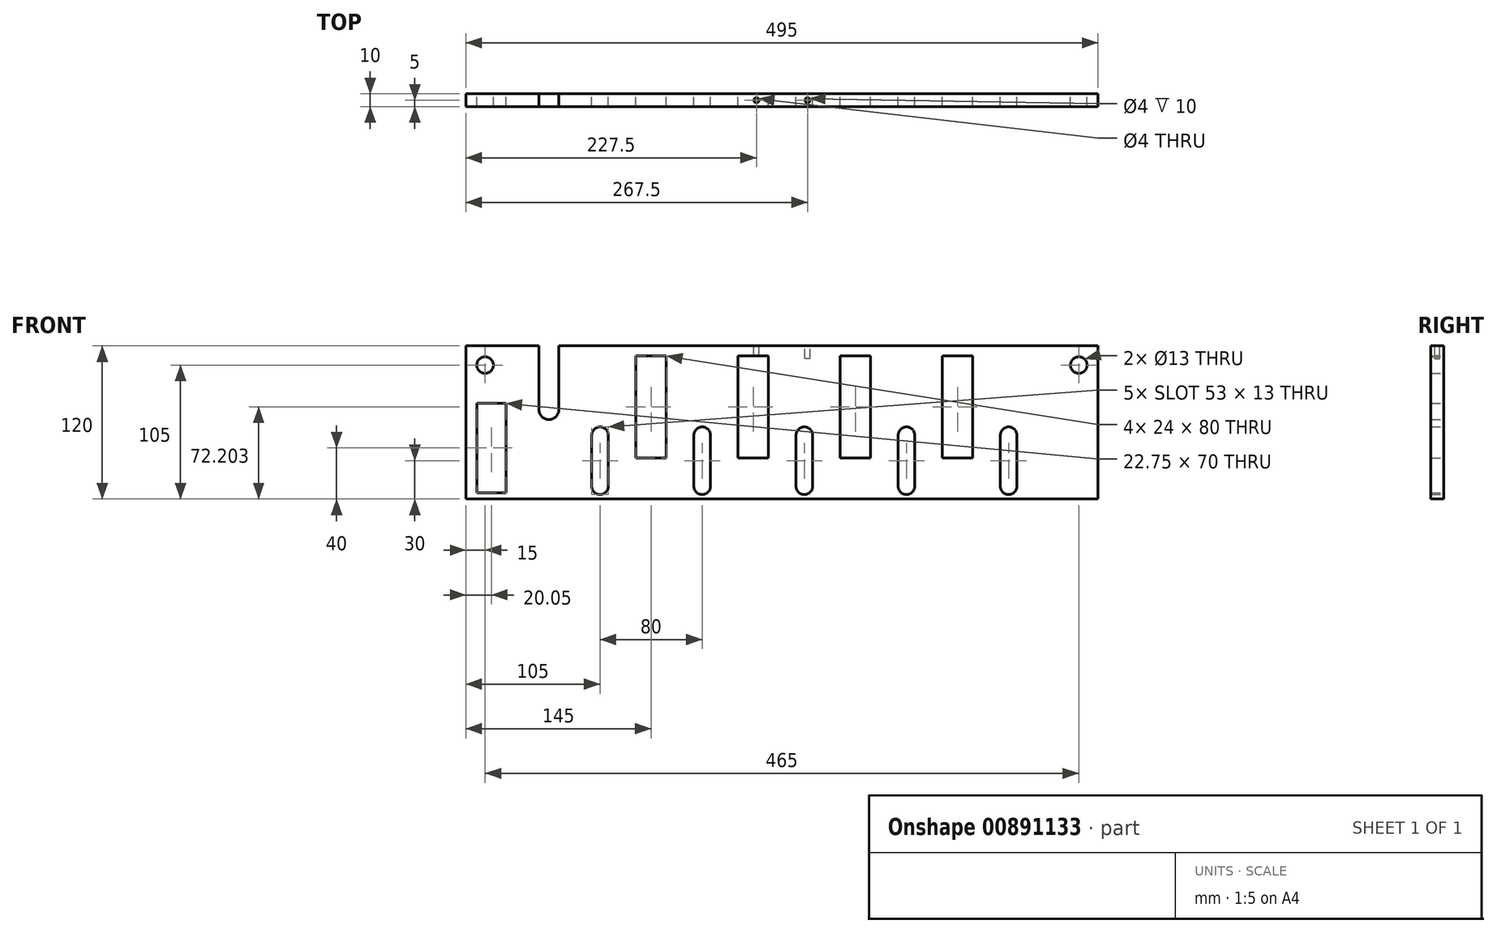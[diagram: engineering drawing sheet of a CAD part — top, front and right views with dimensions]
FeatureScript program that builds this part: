
annotation { "Feature Type Name" : "Feature", "Feature Type Description" : "" }
export const myFeature = defineFeature(function(context is Context, id is Id, definition is map)
    precondition{}
    {
        {
            var Q0;
            Q0=qCreatedBy(makeId("Front.planeOp"),FACE);
            var sketch = newSketch(context, id + "F0", { "sketchPlane" : qUnion([Q0])});
            skLineSegment(sketch, "E0.bottom", {"start": v(-247.5, -60) * mm, "end": v(247.5, -60) * mm});
            skLineSegment(sketch, "E0.top", {"start": v(-247.5, 60) * mm, "end": v(-190.25, 60) * mm});
            skLineSegment(sketch, "E0.left", {"start": v(-247.5, -60) * mm, "end": v(-247.5, 60) * mm});
            skLineSegment(sketch, "E0.right", {"start": v(247.5, -60) * mm, "end": v(247.5, 60) * mm});
            skPoint(sketch, "E0.middle", {"position": v(0, 0) * mm});
            skLineSegment(sketch, "E1", {"start": v(137.5, 131.84) * mm, "end": v(137.5, -217.37) * mm, "construction": true});
            skLineSegment(sketch, "E2", {"start": v(57.5, 134.02) * mm, "end": v(57.5, -137.51) * mm, "construction": true});
            skLineSegment(sketch, "E3", {"start": v(-22.5, 142.94) * mm, "end": v(-22.5, -137.01) * mm, "construction": true});
            skLineSegment(sketch, "E4", {"start": v(-102.5, 134.31) * mm, "end": v(-102.5, -207.96) * mm, "construction": true});
            skLineSegment(sketch, "E5.MirrorCS", {"start": v(137.5, 142.94) * mm, "end": v(137.5, -137.01) * mm, "construction": true});
            skArc(sketch, "E6", {"start": v(-190.25, 10) * mm, "mid": v(-182.5, 2.25) * mm, "end": v(-174.75, 10) * mm});
            skLineSegment(sketch, "E7", {"start": v(-190.25, 10) * mm, "end": v(-190.25, 60) * mm});
            skLineSegment(sketch, "E8", {"start": v(-174.75, 10) * mm, "end": v(-174.75, 60) * mm});
            skLineSegment(sketch, "E9", {"start": v(-149, -50) * mm, "end": v(-149, -10) * mm});
            skLineSegment(sketch, "E10", {"start": v(-136, -50) * mm, "end": v(-136, -10) * mm});
            skArc(sketch, "E11", {"start": v(-149, -10) * mm, "mid": v(-142.5, -3.5) * mm, "end": v(-136, -10) * mm});
            skArc(sketch, "E12", {"start": v(-149, -50) * mm, "mid": v(-142.5, -56.5) * mm, "end": v(-136, -50) * mm});
            skLineSegment(sketch, "E13.MirrorCS", {"start": v(-69, -50) * mm, "end": v(-69, -10) * mm});
            skArc(sketch, "E14.MirrorCS", {"start": v(-56, -10) * mm, "mid": v(-62.5, -3.5) * mm, "end": v(-69, -10) * mm});
            skLineSegment(sketch, "E15.MirrorCS", {"start": v(-56, -50) * mm, "end": v(-56, -10) * mm});
            skArc(sketch, "E16.MirrorCS", {"start": v(-56, -50) * mm, "mid": v(-62.5, -56.5) * mm, "end": v(-69, -50) * mm});
            skLineSegment(sketch, "E17.MirrorCS", {"start": v(11, -50) * mm, "end": v(11, -10) * mm});
            skLineSegment(sketch, "E18.MirrorCS", {"start": v(24, -50) * mm, "end": v(24, -10) * mm});
            skArc(sketch, "E19.MirrorCS", {"start": v(11, -10) * mm, "mid": v(17.5, -3.5) * mm, "end": v(24, -10) * mm});
            skArc(sketch, "E20.MirrorCS", {"start": v(11, -50) * mm, "mid": v(17.5, -56.5) * mm, "end": v(24, -50) * mm});
            skArc(sketch, "E21.MirrorCS", {"start": v(104, -10) * mm, "mid": v(97.5, -3.5) * mm, "end": v(91, -10) * mm});
            skLineSegment(sketch, "E22.MirrorCS", {"start": v(91, -50) * mm, "end": v(91, -10) * mm});
            skArc(sketch, "E23.MirrorCS", {"start": v(104, -50) * mm, "mid": v(97.5, -56.5) * mm, "end": v(91, -50) * mm});
            skLineSegment(sketch, "E24.MirrorCS", {"start": v(104, -50) * mm, "end": v(104, -10) * mm});
            skLineSegment(sketch, "E25.MirrorCS", {"start": v(171, -50) * mm, "end": v(171, -10) * mm});
            skLineSegment(sketch, "E26.MirrorCS", {"start": v(184, -50) * mm, "end": v(184, -10) * mm});
            skArc(sketch, "E27.MirrorCS", {"start": v(171, -10) * mm, "mid": v(177.5, -3.5) * mm, "end": v(184, -10) * mm});
            skArc(sketch, "E28.MirrorCS", {"start": v(171, -50) * mm, "mid": v(177.5, -56.5) * mm, "end": v(184, -50) * mm});
            skLineSegment(sketch, "E29.trimOffspring", {"start": v(-174.75, 60) * mm, "end": v(247.5, 60) * mm});
            skCircle(sketch, "E30", {"center": v(-232.5, 45) * mm, "radius": 6.5 * mm});
            skLineSegment(sketch, "E31", {"start": v(0, 134.05) * mm, "end": v(0, -133.19) * mm, "construction": true});
            skCircle(sketch, "E32.MirrorC", {"center": v(232.5, 45) * mm, "radius": 6.5 * mm});
            skLineSegment(sketch, "E33.bottom", {"start": v(-114.5, -27.8) * mm, "end": v(-90.5, -27.8) * mm});
            skLineSegment(sketch, "E33.top", {"start": v(-114.5, 52.2) * mm, "end": v(-90.5, 52.2) * mm});
            skLineSegment(sketch, "E33.left", {"start": v(-114.5, -27.8) * mm, "end": v(-114.5, 52.2) * mm});
            skLineSegment(sketch, "E33.right", {"start": v(-90.5, -27.8) * mm, "end": v(-90.5, 52.2) * mm});
            skPoint(sketch, "E33.middle", {"position": v(-102.5, 12.2) * mm});
            skLineSegment(sketch, "E34.bottom", {"start": v(-34.5, -27.8) * mm, "end": v(-10.5, -27.8) * mm});
            skLineSegment(sketch, "E34.top", {"start": v(-34.5, 52.2) * mm, "end": v(-10.5, 52.2) * mm});
            skLineSegment(sketch, "E34.left", {"start": v(-34.5, -27.8) * mm, "end": v(-34.5, 52.2) * mm});
            skLineSegment(sketch, "E34.right", {"start": v(-10.5, -27.8) * mm, "end": v(-10.5, 52.2) * mm});
            skPoint(sketch, "E34.middle", {"position": v(-22.5, 12.2) * mm});
            skLineSegment(sketch, "E35.bottom", {"start": v(45.5, -27.8) * mm, "end": v(69.5, -27.8) * mm});
            skLineSegment(sketch, "E35.top", {"start": v(45.5, 52.2) * mm, "end": v(69.5, 52.2) * mm});
            skLineSegment(sketch, "E35.left", {"start": v(45.5, -27.8) * mm, "end": v(45.5, 52.2) * mm});
            skLineSegment(sketch, "E35.right", {"start": v(69.5, -27.8) * mm, "end": v(69.5, 52.2) * mm});
            skPoint(sketch, "E35.middle", {"position": v(57.5, 12.2) * mm});
            skLineSegment(sketch, "E36.bottom", {"start": v(125.5, -27.8) * mm, "end": v(149.5, -27.8) * mm});
            skLineSegment(sketch, "E36.top", {"start": v(125.5, 52.2) * mm, "end": v(149.5, 52.2) * mm});
            skLineSegment(sketch, "E36.left", {"start": v(125.5, -27.8) * mm, "end": v(125.5, 52.2) * mm});
            skLineSegment(sketch, "E36.right", {"start": v(149.5, -27.8) * mm, "end": v(149.5, 52.2) * mm});
            skPoint(sketch, "E36.middle", {"position": v(137.5, 12.2) * mm});
            skLineSegment(sketch, "E37.bottom", {"start": v(-238.82, 15) * mm, "end": v(-216.08, 15) * mm});
            skLineSegment(sketch, "E37.top", {"start": v(-238.82, -55) * mm, "end": v(-216.08, -55) * mm});
            skLineSegment(sketch, "E37.left", {"start": v(-238.82, 15) * mm, "end": v(-238.82, -55) * mm});
            skLineSegment(sketch, "E37.right", {"start": v(-216.08, 15) * mm, "end": v(-216.08, -55) * mm});
            skPoint(sketch, "E37.middle", {"position": v(-227.45, -20) * mm});
            skSolve(sketch);
        }
        {
            var Q0;
            Q0 = qSketchRegion(id + "F0", true);
            extrude(context, id + "F1", {"entities" : qUnion([Q0]), "endBound" : BoundingType.SYMMETRIC, "depth" : 10 * mm, "offsetDistance" : 25 * mm});
        }
        {
            var Q0;
            Q0=makeQuery(id+"F1.opExtrude","SWEPT_FACE",FACE,{"disambiguationData":[OSD([sQuery(id+"F0.wireOp",EDGE,"E29.trimOffspring")])]});
            var sketch = newSketch(context, id + "F2", { "sketchPlane" : qUnion([Q0])});
            skCircle(sketch, "E38", {"center": v(-20, 0) * mm, "radius": 2 * mm});
            skLineSegment(sketch, "E39", {"start": v(0, 40.55) * mm, "end": v(0, -47.78) * mm, "construction": true});
            skCircle(sketch, "E40.MirrorC", {"center": v(20, 0) * mm, "radius": 2 * mm});
            skSolve(sketch);
        }
        {
            var Q0;
            Q0 = qSketchRegion(id + "F2", true);
            extrude(context, id + "F3", {"entities" : qUnion([Q0]), "operationType" : NewBodyOperationType.REMOVE, "oppositeDirection" : true, "depth" : 10 * mm, "offsetDistance" : 25 * mm});
        }
    });
